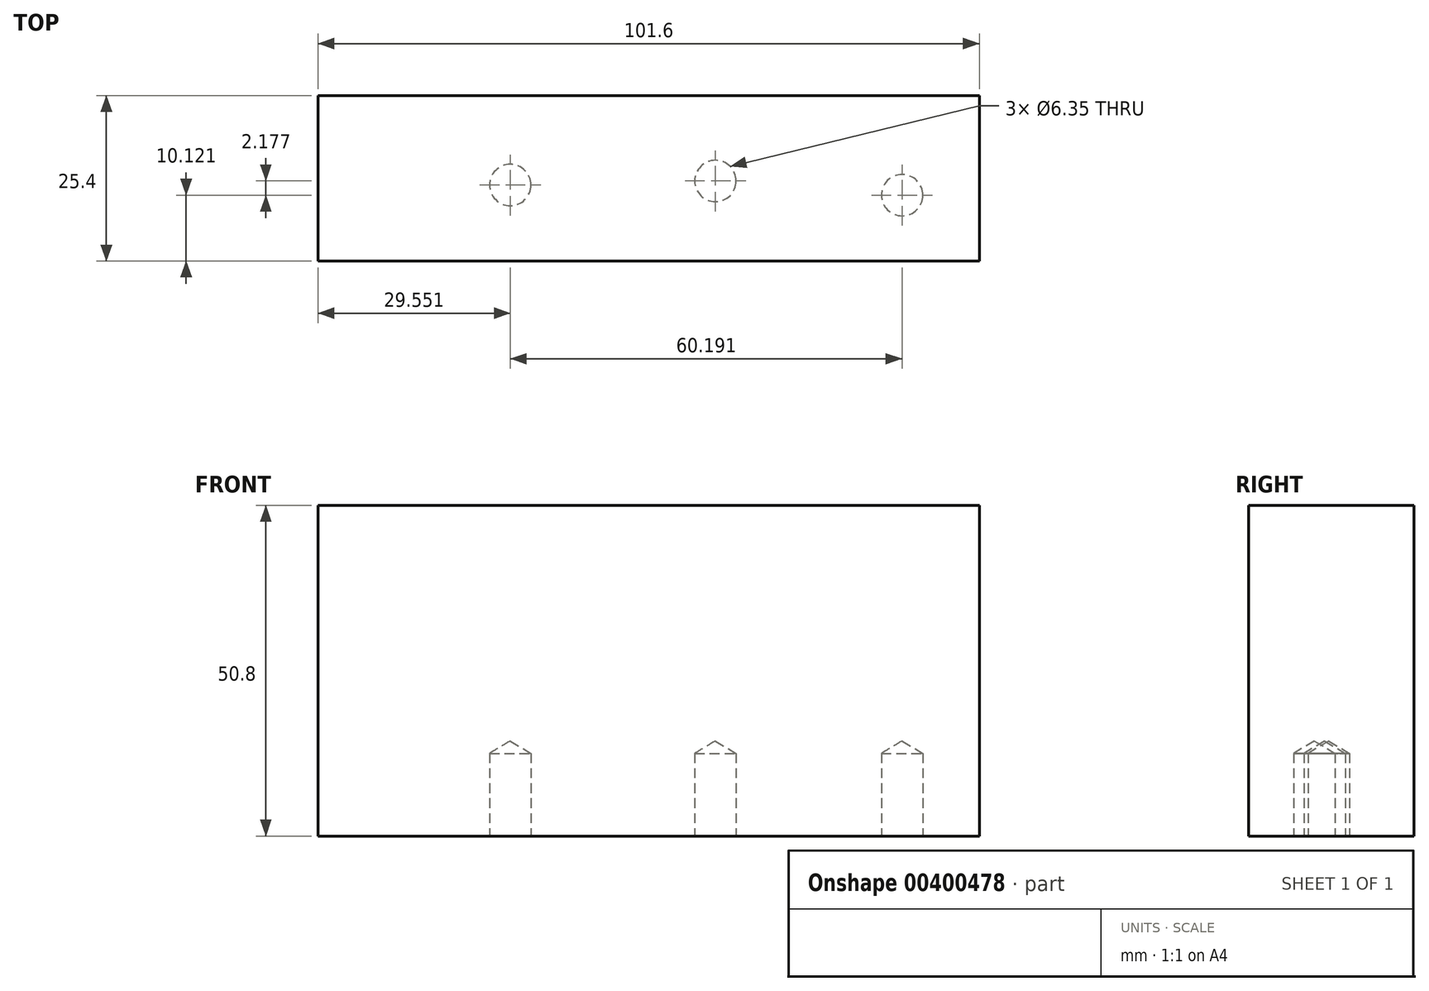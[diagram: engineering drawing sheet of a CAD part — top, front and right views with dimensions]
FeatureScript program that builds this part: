
annotation { "Feature Type Name" : "Feature", "Feature Type Description" : "" }
export const myFeature = defineFeature(function(context is Context, id is Id, definition is map)
    precondition{}
    {
        {
            var Q0;
            Q0=qCreatedBy(makeId("Front.planeOp"),FACE);
            var sketch = newSketch(context, id + "F0", { "sketchPlane" : qUnion([Q0])});
            skLineSegment(sketch, "E0.bottom", {"start": v(0, 50.8) * mm, "end": v(101.6, 50.8) * mm});
            skLineSegment(sketch, "E0.top", {"start": v(0, 0) * mm, "end": v(101.6, 0) * mm});
            skLineSegment(sketch, "E0.left", {"start": v(0, 50.8) * mm, "end": v(0, 0) * mm});
            skLineSegment(sketch, "E0.right", {"start": v(101.6, 50.8) * mm, "end": v(101.6, 0) * mm});
            skSolve(sketch);
        }
        {
            var Q0;
            Q0 = qSketchRegion(id + "F0", true);
            extrude(context, id + "F1", {"entities" : qUnion([Q0]), "depth" : 25.4 * mm});
        }
        {
            var Q0;
            Q0=makeQuery(id+"F1.opExtrude","SWEPT_FACE",FACE,{"disambiguationData":[OSD([sQuery(id+"F0.wireOp",EDGE,"E0.top")])]});
            var sketch = newSketch(context, id + "F2", { "sketchPlane" : qUnion([Q0])});
            skPoint(sketch, "E1", {"position": v(89.74, 15.28) * mm});
            skPoint(sketch, "E2", {"position": v(61.06, 13.1) * mm});
            skPoint(sketch, "E3", {"position": v(29.55, 13.72) * mm});
            skSolve(sketch);
        }
        {
            var Q0;
            Q0=sQuery(id+"F2.wireOp",VERTEX,"E2");
            var Q1;
            Q1=sQuery(id+"F2.wireOp",VERTEX,"E3");
            var Q2;
            Q2=sQuery(id+"F2.wireOp",VERTEX,"E1");
            var Q3;
            Q3=makeQuery(id+"F1.opExtrude","SWEPT_BODY",BODY,{"disambiguationData":[OSD([sQuery(id+"F0.wireOp",EDGE,"E0.bottom"),sQuery(id+"F0.wireOp",EDGE,"E0.top"),sQuery(id+"F0.wireOp",EDGE,"E0.left"),sQuery(id+"F0.wireOp",EDGE,"E0.right")])]});
            hole(context, id + "F3", {"style" : HoleStyle.SIMPLE, "endStyle" : HoleEndStyle.BLIND, "holeDiameter" : 6.35 * mm, "holeDepth" : 12.7 * mm, "isTappedThrough" : true, "tappedDepth" : 12.7 * mm, "tapClearance" : 3, "locations" : qUnion([Q0, Q1, Q2]), "scope" : qUnion([Q3])});
        }
        {
            var Q0;
            Q0=makeQuery(id+"F1.opExtrude","SWEPT_FACE",FACE,{"disambiguationData":[OSD([sQuery(id+"F0.wireOp",EDGE,"E0.top")])]});
            var Q1;
            Q1=makeQuery(id+"F1.opExtrude","SWEPT_FACE",FACE,{"disambiguationData":[OSD([sQuery(id+"F0.wireOp",EDGE,"E0.bottom")])]});
            cPlane(context, id + "F4", {"entities" : qUnion([Q0, Q1]), "cplaneType" : CPlaneType.MID_PLANE, "offset" : 25.4 * mm, "width" : 152.4 * mm, "height" : 152.4 * mm});
        }
    });
